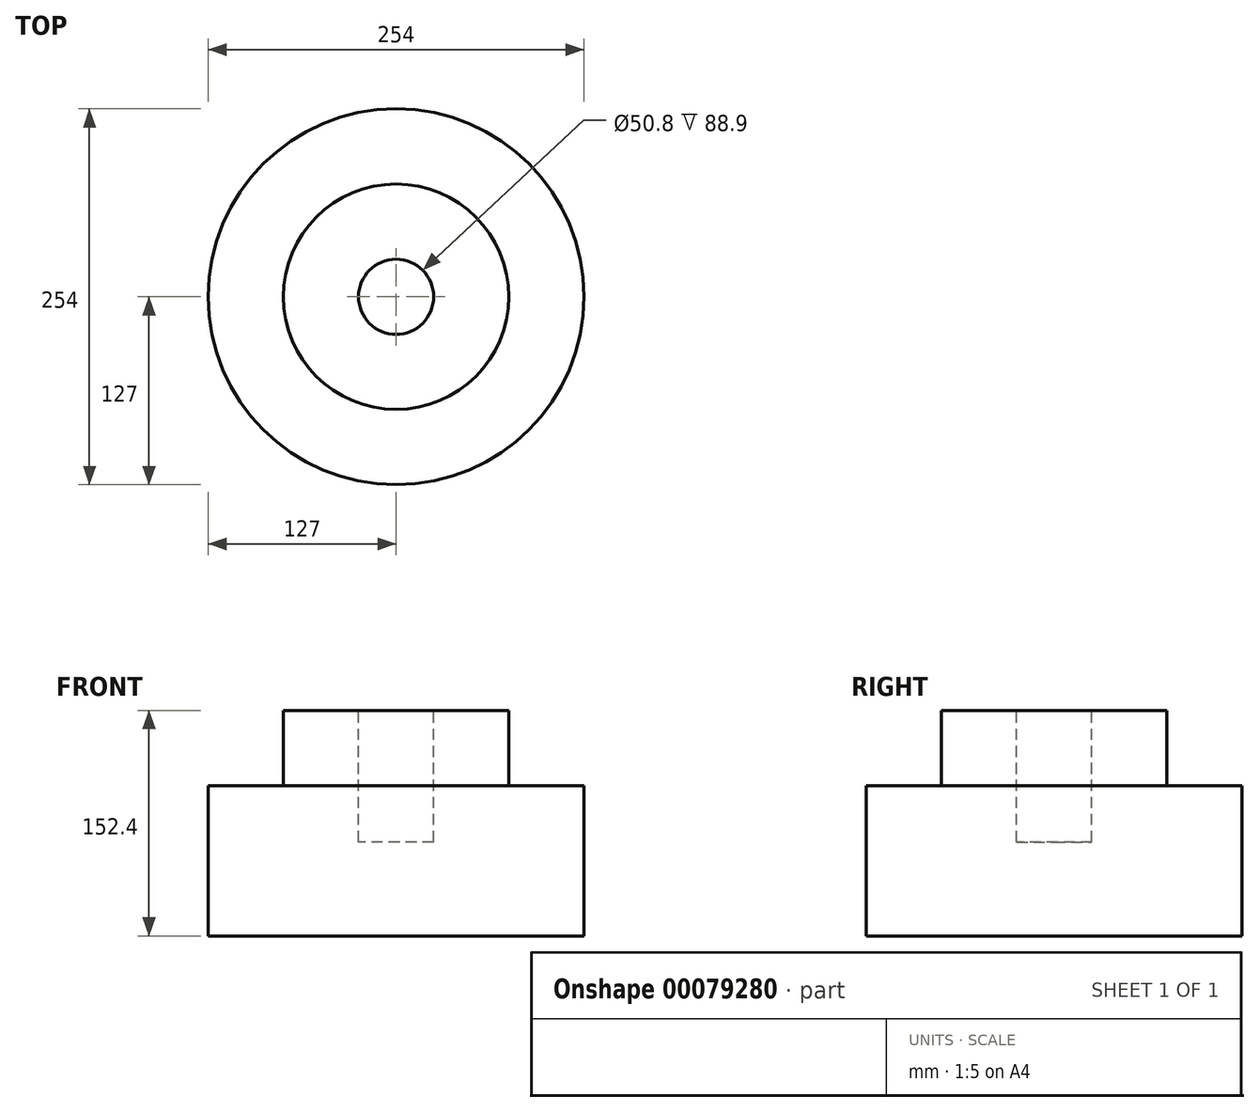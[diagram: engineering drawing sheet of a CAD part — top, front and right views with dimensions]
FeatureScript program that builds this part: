
annotation { "Feature Type Name" : "Feature", "Feature Type Description" : "" }
export const myFeature = defineFeature(function(context is Context, id is Id, definition is map)
    precondition{}
    {
        {
            var Q0;
            Q0=qCreatedBy(makeId("Front.planeOp"),FACE);
            var sketch = newSketch(context, id + "F0", { "sketchPlane" : qUnion([Q0])});
            skLineSegment(sketch, "E0", {"start": v(0, 64.4) * mm, "end": v(0, 0.9) * mm});
            skLineSegment(sketch, "E1", {"start": v(0, 0.9) * mm, "end": v(127, 0.9) * mm});
            skLineSegment(sketch, "E2", {"start": v(127, 0.9) * mm, "end": v(127, 102.5) * mm});
            skLineSegment(sketch, "E3", {"start": v(127, 102.5) * mm, "end": v(76.2, 102.5) * mm});
            skLineSegment(sketch, "E4", {"start": v(76.2, 102.5) * mm, "end": v(76.2, 153.3) * mm});
            skLineSegment(sketch, "E5", {"start": v(76.2, 153.3) * mm, "end": v(25.4, 153.3) * mm});
            skLineSegment(sketch, "E6", {"start": v(25.4, 153.3) * mm, "end": v(25.4, 64.4) * mm});
            skLineSegment(sketch, "E7", {"start": v(25.4, 64.4) * mm, "end": v(0, 64.4) * mm});
            skSolve(sketch);
        }
        {
            var Q0;
            Q0=makeQuery(id+"F0.imprint","IMPRINT",FACE,{"disambiguationData":[TD([[makeQuery(id+"F0.imprint","IMPRINT",EDGE,{"derivedFrom":sQuery(id+"F0.wireOp",EDGE,"E0")}),1.0]])]});
            var Q1;
            Q1=sQuery(id+"F0.wireOp",EDGE,"E0");
            revolve(context, id + "F1", {"entities" : qUnion([Q0]), "axis" : qUnion([Q1]), "revolveType" : RevolveType.FULL});
        }
    });
